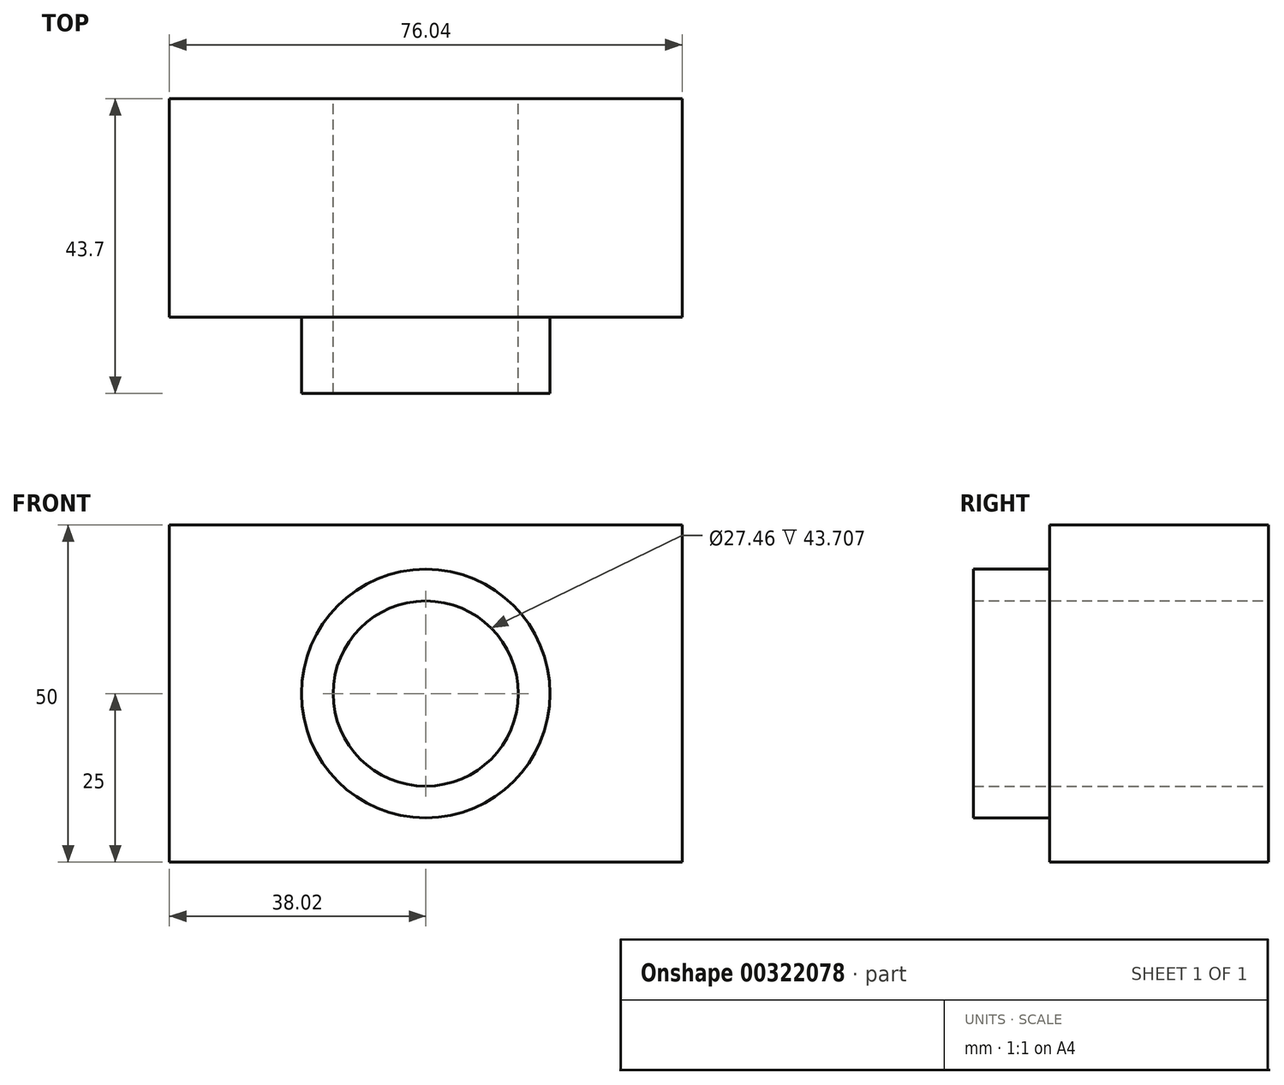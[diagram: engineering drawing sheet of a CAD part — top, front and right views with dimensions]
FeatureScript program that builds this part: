
annotation { "Feature Type Name" : "Feature", "Feature Type Description" : "" }
export const myFeature = defineFeature(function(context is Context, id is Id, definition is map)
    precondition{}
    {
        {
            var Q0;
            Q0=qCreatedBy(makeId("Top.planeOp"),FACE);
            var sketch = newSketch(context, id + "F0", { "sketchPlane" : qUnion([Q0])});
            skLineSegment(sketch, "E0.bottom", {"start": v(38.02, -16.2) * mm, "end": v(-38.02, -16.2) * mm});
            skLineSegment(sketch, "E0.top", {"start": v(38.02, 16.2) * mm, "end": v(-38.02, 16.2) * mm});
            skLineSegment(sketch, "E0.left", {"start": v(38.02, -16.2) * mm, "end": v(38.02, 16.2) * mm});
            skLineSegment(sketch, "E0.right", {"start": v(-38.02, -16.2) * mm, "end": v(-38.02, 16.2) * mm});
            skPoint(sketch, "E0.middle", {"position": v(0, 0) * mm});
            skSolve(sketch);
        }
        {
            var Q0;
            Q0=makeQuery(id+"F0.imprint","IMPRINT",FACE,{"disambiguationData":[TD([[makeQuery(id+"F0.imprint","IMPRINT",EDGE,{"derivedFrom":sQuery(id+"F0.wireOp",EDGE,"E0.bottom")}),-1.0]])]});
            extrude(context, id + "F1", {"entities" : qUnion([Q0]), "depth" : 25 * mm, "hasSecondDirection" : true, "secondDirectionOppositeDirection" : true, "secondDirectionDepth" : 25 * mm});
        }
        {
            var Q0;
            Q0=makeQuery(id+"F1.opExtrude","SWEPT_FACE",FACE,{"disambiguationData":[OSD([sQuery(id+"F0.wireOp",EDGE,"E0.bottom")])]});
            var sketch = newSketch(context, id + "F2", { "sketchPlane" : qUnion([Q0])});
            skCircle(sketch, "E1", {"center": v(0, 0) * mm, "radius": 18.43 * mm});
            skCircle(sketch, "E2", {"center": v(0, 0) * mm, "radius": 13.73 * mm});
            skSolve(sketch);
        }
        {
            var Q0;
            Q0=makeQuery(id+"F2.imprint","IMPRINT",FACE,{"disambiguationData":[TD([[makeQuery(id+"F2.imprint","IMPRINT",EDGE,{"derivedFrom":sQuery(id+"F2.wireOp",EDGE,"E1")}),1.0]])]});
            extrude(context, id + "F3", {"entities" : qUnion([Q0]), "operationType" : NewBodyOperationType.ADD, "depth" : 11.3 * mm});
        }
        {
            var Q0;
            Q0=makeQuery(id+"F3.boolean.opBoolean","SPLIT",FACE,{"disambiguationData":[TD([makeQuery(id+"F3.opExtrude","SWEPT_FACE",FACE,{"disambiguationData":[OSD([sQuery(id+"F2.wireOp",EDGE,"E2")])]})])],"derivedFrom":makeQuery(id+"F1.opExtrude","SWEPT_FACE",FACE,{"disambiguationData":[OSD([sQuery(id+"F0.wireOp",EDGE,"E0.bottom")])]})});
            var Q1;
            Q1=makeQuery(id+"F1.opExtrude","SWEPT_FACE",FACE,{"disambiguationData":[OSD([sQuery(id+"F0.wireOp",EDGE,"E0.top")])]});
            extrude(context, id + "F4", {"entities" : qUnion([Q0]), "operationType" : NewBodyOperationType.REMOVE, "endBound" : BoundingType.UP_TO_SURFACE, "oppositeDirection" : true, "endBoundEntityFace" : qUnion([Q1]), "depth" : 53.1 * mm});
        }
    });
